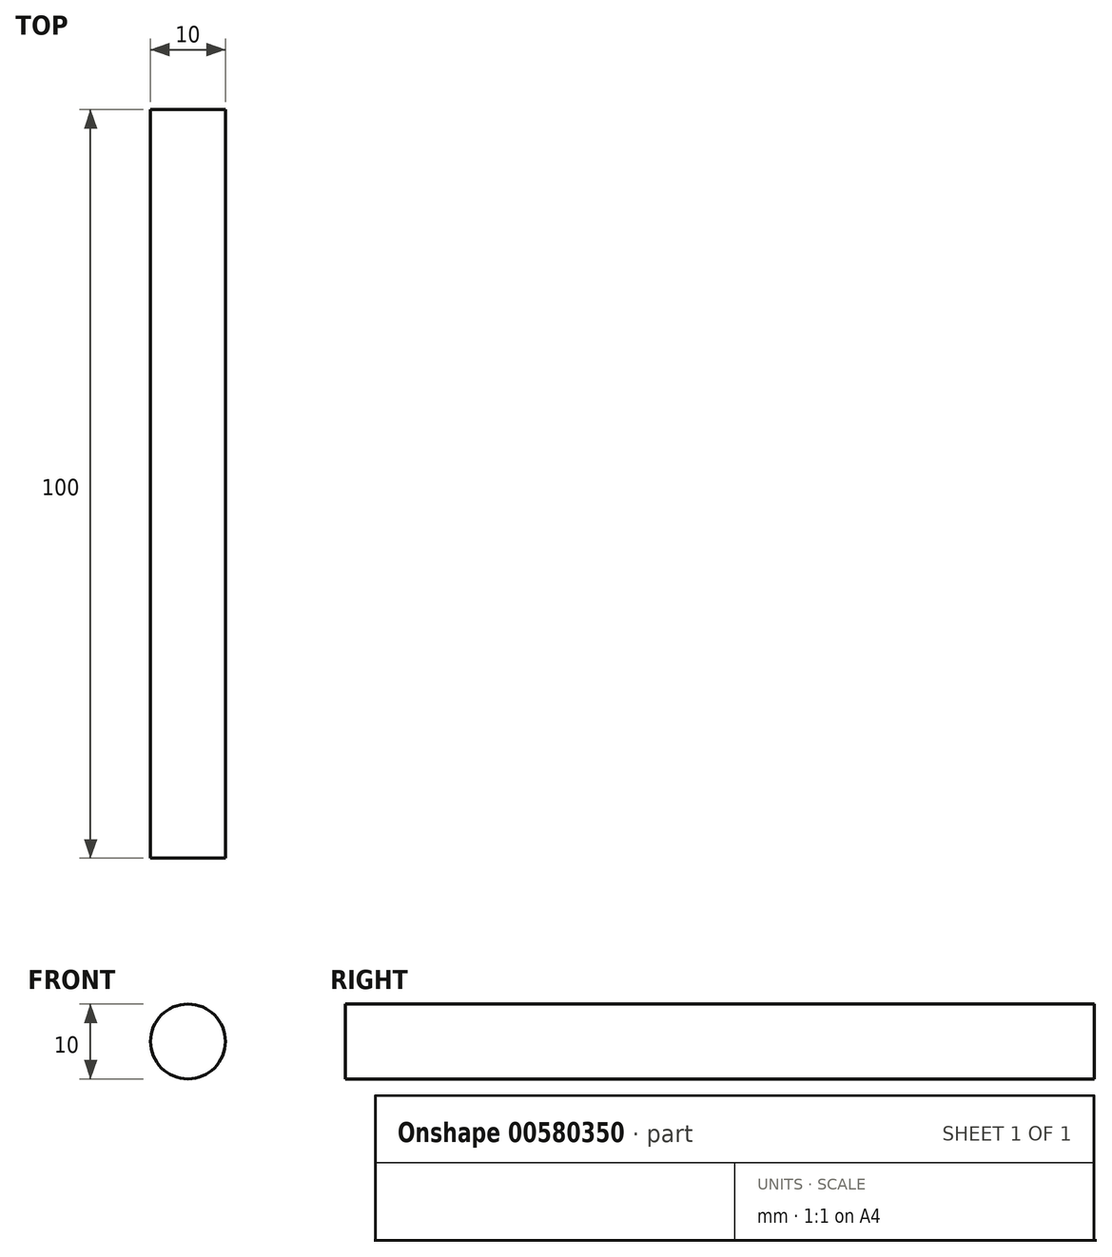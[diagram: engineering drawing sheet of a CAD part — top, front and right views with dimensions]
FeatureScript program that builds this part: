
annotation { "Feature Type Name" : "Feature", "Feature Type Description" : "" }
export const myFeature = defineFeature(function(context is Context, id is Id, definition is map)
    precondition{}
    {
        {
            assignVariable(context, id + "F0", {"name" : "axleDepth", "anyValue" : 100});
        }
        {
            var Q0;
            Q0=qCreatedBy(makeId("Front.planeOp"),FACE);
            var sketch = newSketch(context, id + "F1", { "sketchPlane" : qUnion([Q0])});
            skCircle(sketch, "E0", {"center": v(0, 0) * mm, "radius": 5 * mm});
            skSolve(sketch);
        }
        {
            var Q0;
            Q0=makeQuery(id+"F1.imprint","IMPRINT",FACE,{"disambiguationData":[TD([[makeQuery(id+"F1.imprint","IMPRINT",EDGE,{"derivedFrom":sQuery(id+"F1.wireOp",EDGE,"E0")}),1.0]])]});
            extrude(context, id + "F2", {"entities" : qUnion([Q0]), "depth" : (getVariable(context, 'axleDepth')) * mm, "offsetDistance" : 25 * mm});
        }
    });
